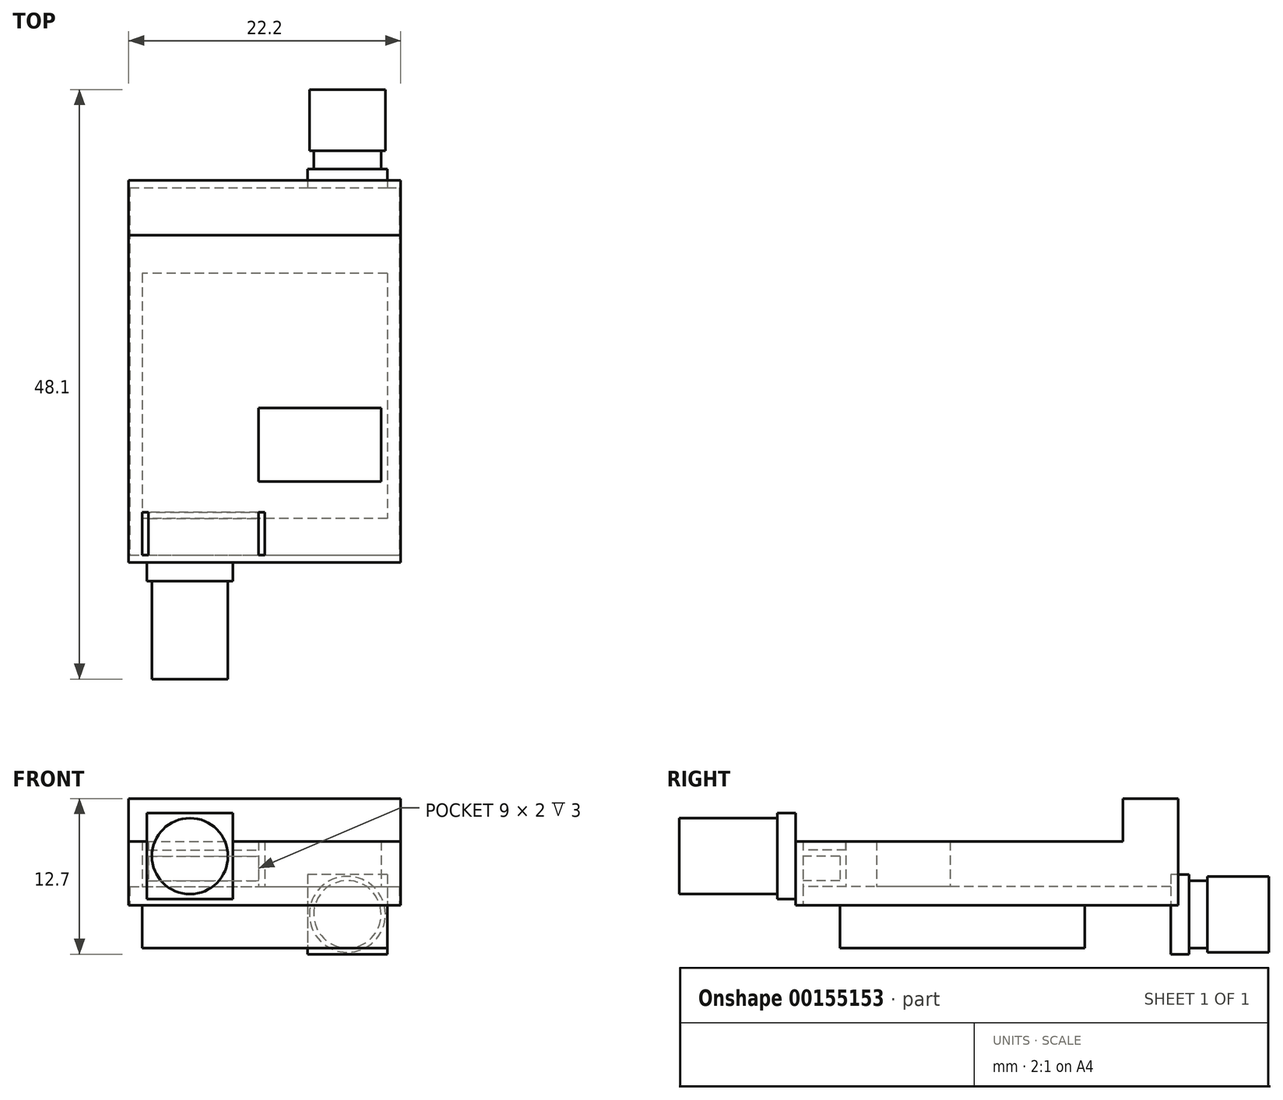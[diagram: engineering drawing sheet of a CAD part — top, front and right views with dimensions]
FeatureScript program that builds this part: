
annotation { "Feature Type Name" : "Feature", "Feature Type Description" : "" }
export const myFeature = defineFeature(function(context is Context, id is Id, definition is map)
    precondition{}
    {
        {
            var Q0;
            Q0=qCreatedBy(makeId("Top.planeOp"),FACE);
            var sketch = newSketch(context, id + "F0", { "sketchPlane" : qUnion([Q0])});
            skLineSegment(sketch, "E0.bottom", {"start": v(-11, 15) * mm, "end": v(11, 15) * mm});
            skLineSegment(sketch, "E0.top", {"start": v(-11, -15) * mm, "end": v(11, -15) * mm});
            skLineSegment(sketch, "E0.left", {"start": v(-11, 15) * mm, "end": v(-11, -15) * mm});
            skLineSegment(sketch, "E0.right", {"start": v(11, 15) * mm, "end": v(11, -15) * mm});
            skSolve(sketch);
        }
        {
            var Q0;
            Q0=makeQuery(id+"F0.imprint","IMPRINT",FACE,{"disambiguationData":[TD([[makeQuery(id+"F0.imprint","IMPRINT",EDGE,{"derivedFrom":sQuery(id+"F0.wireOp",EDGE,"E0.bottom")}),-1.0]])]});
            extrude(context, id + "F1", {"entities" : qUnion([Q0]), "depth" : 1.5 * mm});
        }
        {
            var Q0;
            Q0=makeQuery(id+"F1.opExtrude","SWEPT_FACE",FACE,{"disambiguationData":[OSD([sQuery(id+"F0.wireOp",EDGE,"E0.bottom")])]});
            var sketch = newSketch(context, id + "F2", { "sketchPlane" : qUnion([Q0])});
            skLineSegment(sketch, "E1.bottom", {"start": v(-10, 2.5) * mm, "end": v(-3.5, 2.5) * mm});
            skLineSegment(sketch, "E1.top", {"start": v(-10, -4) * mm, "end": v(-3.5, -4) * mm});
            skLineSegment(sketch, "E1.left", {"start": v(-10, 2.5) * mm, "end": v(-10, -4) * mm});
            skLineSegment(sketch, "E1.right", {"start": v(-3.5, 2.5) * mm, "end": v(-3.5, -4) * mm});
            skSolve(sketch);
        }
        {
            var Q0;
            Q0 = qSketchRegion(id + "F2", true);
            extrude(context, id + "F3", {"entities" : qUnion([Q0]), "operationType" : NewBodyOperationType.ADD, "depth" : 1.5 * mm});
        }
        {
            var Q0;
            Q0=makeQuery(id+"F3.opExtrude","CAP_FACE",FACE,{"disambiguationData":[OSD([sQuery(id+"F2.wireOp",EDGE,"E1.bottom"),sQuery(id+"F2.wireOp",EDGE,"E1.top"),sQuery(id+"F2.wireOp",EDGE,"E1.left"),sQuery(id+"F2.wireOp",EDGE,"E1.right")])],"isStart":false});
            var sketch = newSketch(context, id + "F4", { "sketchPlane" : qUnion([Q0])});
            skCircle(sketch, "E2", {"center": v(-6.75, -0.75) * mm, "radius": 2.75 * mm});
            skPoint(sketch, "E2.centerSnap0", {"position": v(-6.75, -4) * mm});
            skSolve(sketch);
        }
        {
            var Q0;
            Q0 = qSketchRegion(id + "F4", true);
            extrude(context, id + "F5", {"entities" : qUnion([Q0]), "operationType" : NewBodyOperationType.ADD, "depth" : 1.5 * mm});
        }
        {
            var Q0;
            Q0=makeQuery(id+"F5.opExtrude","CAP_FACE",FACE,{"disambiguationData":[OSD([sQuery(id+"F4.wireOp",EDGE,"E2")])],"isStart":false});
            var sketch = newSketch(context, id + "F6", { "sketchPlane" : qUnion([Q0])});
            skCircle(sketch, "E3", {"center": v(-6.75, -0.75) * mm, "radius": 3.1 * mm});
            skSolve(sketch);
        }
        {
            var Q0;
            Q0 = qSketchRegion(id + "F6", true);
            extrude(context, id + "F7", {"entities" : qUnion([Q0]), "operationType" : NewBodyOperationType.ADD, "depth" : 5 * mm});
        }
        {
            var Q0;
            Q0=makeQuery(id+"F1.opExtrude","CAP_FACE",FACE,{"disambiguationData":[OSD([sQuery(id+"F0.wireOp",EDGE,"E0.bottom"),sQuery(id+"F0.wireOp",EDGE,"E0.top"),sQuery(id+"F0.wireOp",EDGE,"E0.left"),sQuery(id+"F0.wireOp",EDGE,"E0.right")])],"isStart":true});
            var sketch = newSketch(context, id + "F8", { "sketchPlane" : qUnion([Q0])});
            skLineSegment(sketch, "E4.bottom", {"start": v(10, -8) * mm, "end": v(-10, -8) * mm});
            skLineSegment(sketch, "E4.top", {"start": v(10, 12) * mm, "end": v(-10, 12) * mm});
            skLineSegment(sketch, "E4.left", {"start": v(10, -8) * mm, "end": v(10, 12) * mm});
            skLineSegment(sketch, "E4.right", {"start": v(-10, -8) * mm, "end": v(-10, 12) * mm});
            skSolve(sketch);
        }
        {
            var Q0;
            Q0=makeQuery(id+"F8.imprint","IMPRINT",FACE,{"disambiguationData":[TD([[makeQuery(id+"F8.imprint","IMPRINT",EDGE,{"derivedFrom":sQuery(id+"F8.wireOp",EDGE,"E4.bottom")}),-1.0]])]});
            extrude(context, id + "F9", {"entities" : qUnion([Q0]), "operationType" : NewBodyOperationType.ADD, "depth" : 3.5 * mm});
        }
        {
            var Q0;
            Q0=makeQuery(id+"F1.opExtrude","CAP_FACE",FACE,{"disambiguationData":[OSD([sQuery(id+"F0.wireOp",EDGE,"E0.bottom"),sQuery(id+"F0.wireOp",EDGE,"E0.top"),sQuery(id+"F0.wireOp",EDGE,"E0.left"),sQuery(id+"F0.wireOp",EDGE,"E0.right")])],"isStart":false});
            var sketch = newSketch(context, id + "F10", { "sketchPlane" : qUnion([Q0])});
            skLineSegment(sketch, "E5.bottom", {"start": v(-10, -11.5) * mm, "end": v(0, -11.5) * mm});
            skLineSegment(sketch, "E5.top", {"start": v(-10, -15) * mm, "end": v(0, -15) * mm});
            skLineSegment(sketch, "E5.left", {"start": v(-10, -11.5) * mm, "end": v(-10, -15) * mm});
            skLineSegment(sketch, "E5.right", {"start": v(0, -11.5) * mm, "end": v(0, -15) * mm});
            skSolve(sketch);
        }
        {
            var Q0;
            Q0=makeQuery(id+"F10.imprint","IMPRINT",FACE,{"disambiguationData":[TD([[makeQuery(id+"F10.imprint","IMPRINT",EDGE,{"derivedFrom":sQuery(id+"F10.wireOp",EDGE,"E5.bottom")}),-1.0]])]});
            extrude(context, id + "F11", {"entities" : qUnion([Q0]), "operationType" : NewBodyOperationType.ADD, "depth" : 4.5 * mm});
        }
        {
            var Q0;
            Q0=makeQuery(id+"F11.boolean.opBoolean","MERGE",FACE,{"derivedFrom":[makeQuery(id+"F1.opExtrude","SWEPT_FACE",FACE,{"disambiguationData":[OSD([sQuery(id+"F0.wireOp",EDGE,"E0.top")])]}),makeQuery(id+"F11.opExtrude","SWEPT_FACE",FACE,{"disambiguationData":[OSD([sQuery(id+"F10.wireOp",EDGE,"E5.top")])]})]});
            var sketch = newSketch(context, id + "F12", { "sketchPlane" : qUnion([Q0])});
            skLineSegment(sketch, "E6.bottom", {"start": v(-9.5, 5.5) * mm, "end": v(-0.5, 5.5) * mm});
            skLineSegment(sketch, "E6.top", {"start": v(-9.5, 4.5) * mm, "end": v(-0.5, 4.5) * mm});
            skLineSegment(sketch, "E6.left", {"start": v(-9.5, 5.5) * mm, "end": v(-9.5, 4.5) * mm});
            skLineSegment(sketch, "E6.right", {"start": v(-0.5, 5.5) * mm, "end": v(-0.5, 4.5) * mm});
            skLineSegment(sketch, "E7.bottom", {"start": v(-9.5, 4) * mm, "end": v(-0.5, 4) * mm});
            skLineSegment(sketch, "E7.top", {"start": v(-9.5, 2) * mm, "end": v(-0.5, 2) * mm});
            skLineSegment(sketch, "E7.left", {"start": v(-9.5, 4) * mm, "end": v(-9.5, 2) * mm});
            skLineSegment(sketch, "E7.right", {"start": v(-0.5, 4) * mm, "end": v(-0.5, 2) * mm});
            skSolve(sketch);
        }
        {
            var Q0;
            Q0=makeQuery(id+"F12.imprint","IMPRINT",FACE,{"disambiguationData":[TD([[makeQuery(id+"F12.imprint","IMPRINT",EDGE,{"derivedFrom":sQuery(id+"F12.wireOp",EDGE,"E7.bottom")}),-1.0]])]});
            extrude(context, id + "F13", {"entities" : qUnion([Q0]), "operationType" : NewBodyOperationType.REMOVE, "oppositeDirection" : true, "depth" : 3 * mm});
        }
        {
            var Q0;
            Q0=makeQuery(id+"F12.imprint","IMPRINT",FACE,{"disambiguationData":[TD([[makeQuery(id+"F12.imprint","IMPRINT",EDGE,{"derivedFrom":sQuery(id+"F12.wireOp",EDGE,"E6.bottom")}),-1.0]])]});
            extrude(context, id + "F14", {"entities" : qUnion([Q0]), "operationType" : NewBodyOperationType.REMOVE, "oppositeDirection" : true, "depth" : 25 * mm});
        }
        {
            var Q0;
            Q0=makeQuery(id+"F1.opExtrude","CAP_FACE",FACE,{"disambiguationData":[OSD([sQuery(id+"F0.wireOp",EDGE,"E0.bottom"),sQuery(id+"F0.wireOp",EDGE,"E0.top"),sQuery(id+"F0.wireOp",EDGE,"E0.left"),sQuery(id+"F0.wireOp",EDGE,"E0.right")])],"isStart":false});
            var sketch = newSketch(context, id + "F15", { "sketchPlane" : qUnion([Q0])});
            skLineSegment(sketch, "E8.bottom", {"start": v(-0.5, -3) * mm, "end": v(9.5, -3) * mm});
            skLineSegment(sketch, "E8.top", {"start": v(-0.5, -9) * mm, "end": v(9.5, -9) * mm});
            skLineSegment(sketch, "E8.left", {"start": v(-0.5, -3) * mm, "end": v(-0.5, -9) * mm});
            skLineSegment(sketch, "E8.right", {"start": v(9.5, -3) * mm, "end": v(9.5, -9) * mm});
            skSolve(sketch);
        }
        {
            var Q0;
            Q0=makeQuery(id+"F15.imprint","IMPRINT",FACE,{"disambiguationData":[TD([[makeQuery(id+"F15.imprint","IMPRINT",EDGE,{"derivedFrom":sQuery(id+"F15.wireOp",EDGE,"E8.bottom")}),-1.0]])]});
            extrude(context, id + "F16", {"entities" : qUnion([Q0]), "operationType" : NewBodyOperationType.ADD, "depth" : 4 * mm});
        }
        {
            var Q0;
            Q0=qCreatedBy(makeId("Top.planeOp"),FACE);
            var sketch = newSketch(context, id + "F17", { "sketchPlane" : qUnion([Q0])});
            skLineSegment(sketch, "E9.bottom", {"start": v(-11.1, 15.6) * mm, "end": v(11.1, 15.6) * mm});
            skLineSegment(sketch, "E9.top", {"start": v(-11.1, -15.6) * mm, "end": v(11.1, -15.6) * mm});
            skLineSegment(sketch, "E9.left", {"start": v(-11.1, 15.6) * mm, "end": v(-11.1, -15.6) * mm});
            skLineSegment(sketch, "E9.right", {"start": v(11.1, 15.6) * mm, "end": v(11.1, -15.6) * mm});
            skSolve(sketch);
        }
        {
            var Q0;
            Q0 = qSketchRegion(id + "F17", true);
            extrude(context, id + "F18", {"entities" : qUnion([Q0]), "depth" : 8.7 * mm});
        }
        {
            var Q0;
            Q0=makeQuery(id+"F18.opExtrude","SWEPT_FACE",FACE,{"disambiguationData":[OSD([sQuery(id+"F17.wireOp",EDGE,"E9.top")])]});
            var sketch = newSketch(context, id + "F19", { "sketchPlane" : qUnion([Q0])});
            skCircle(sketch, "E10", {"center": v(-6.1, 4) * mm, "radius": 3.1 * mm});
            skSolve(sketch);
        }
        {
            var Q0;
            Q0=makeQuery(id+"F19.imprint","IMPRINT",FACE,{"disambiguationData":[TD([[makeQuery(id+"F19.imprint","IMPRINT",EDGE,{"derivedFrom":sQuery(id+"F19.wireOp",EDGE,"E10")}),1.0]])]});
            extrude(context, id + "F20", {"entities" : qUnion([Q0]), "operationType" : NewBodyOperationType.ADD, "depth" : 9.5 * mm});
        }
        {
            var Q0;
            Q0=makeQuery(id+"F18.opExtrude","CAP_FACE",FACE,{"disambiguationData":[OSD([sQuery(id+"F17.wireOp",EDGE,"E9.bottom"),sQuery(id+"F17.wireOp",EDGE,"E9.top"),sQuery(id+"F17.wireOp",EDGE,"E9.left"),sQuery(id+"F17.wireOp",EDGE,"E9.right")])],"isStart":false});
            var sketch = newSketch(context, id + "F21", { "sketchPlane" : qUnion([Q0])});
            skLineSegment(sketch, "E11.bottom", {"start": v(-11.1, 11.1) * mm, "end": v(11.1, 11.1) * mm});
            skLineSegment(sketch, "E11.top", {"start": v(-11.1, -15.6) * mm, "end": v(11.1, -15.6) * mm});
            skLineSegment(sketch, "E11.left", {"start": v(-11.1, 11.1) * mm, "end": v(-11.1, -15.6) * mm});
            skLineSegment(sketch, "E11.right", {"start": v(11.1, 11.1) * mm, "end": v(11.1, -15.6) * mm});
            skSolve(sketch);
        }
        {
            var Q0;
            Q0 = qSketchRegion(id + "F21", true);
            extrude(context, id + "F22", {"entities" : qUnion([Q0]), "operationType" : NewBodyOperationType.REMOVE, "oppositeDirection" : true, "depth" : 3.5 * mm});
        }
        {
            var Q0;
            Q0=makeQuery(id+"F18.opExtrude","SWEPT_FACE",FACE,{"disambiguationData":[OSD([sQuery(id+"F17.wireOp",EDGE,"E9.top")])]});
            var sketch = newSketch(context, id + "F23", { "sketchPlane" : qUnion([Q0])});
            skLineSegment(sketch, "E12.bottom", {"start": v(-9.6, 7.5) * mm, "end": v(-2.6, 7.5) * mm});
            skLineSegment(sketch, "E12.top", {"start": v(-9.6, 0.5) * mm, "end": v(-2.6, 0.5) * mm});
            skLineSegment(sketch, "E12.left", {"start": v(-9.6, 7.5) * mm, "end": v(-9.6, 0.5) * mm});
            skLineSegment(sketch, "E12.right", {"start": v(-2.6, 7.5) * mm, "end": v(-2.6, 0.5) * mm});
            skSolve(sketch);
        }
        {
            var Q0;
            Q0 = qSketchRegion(id + "F23", true);
            extrude(context, id + "F24", {"entities" : qUnion([Q0]), "operationType" : NewBodyOperationType.ADD, "depth" : 1.5 * mm});
        }
    });
